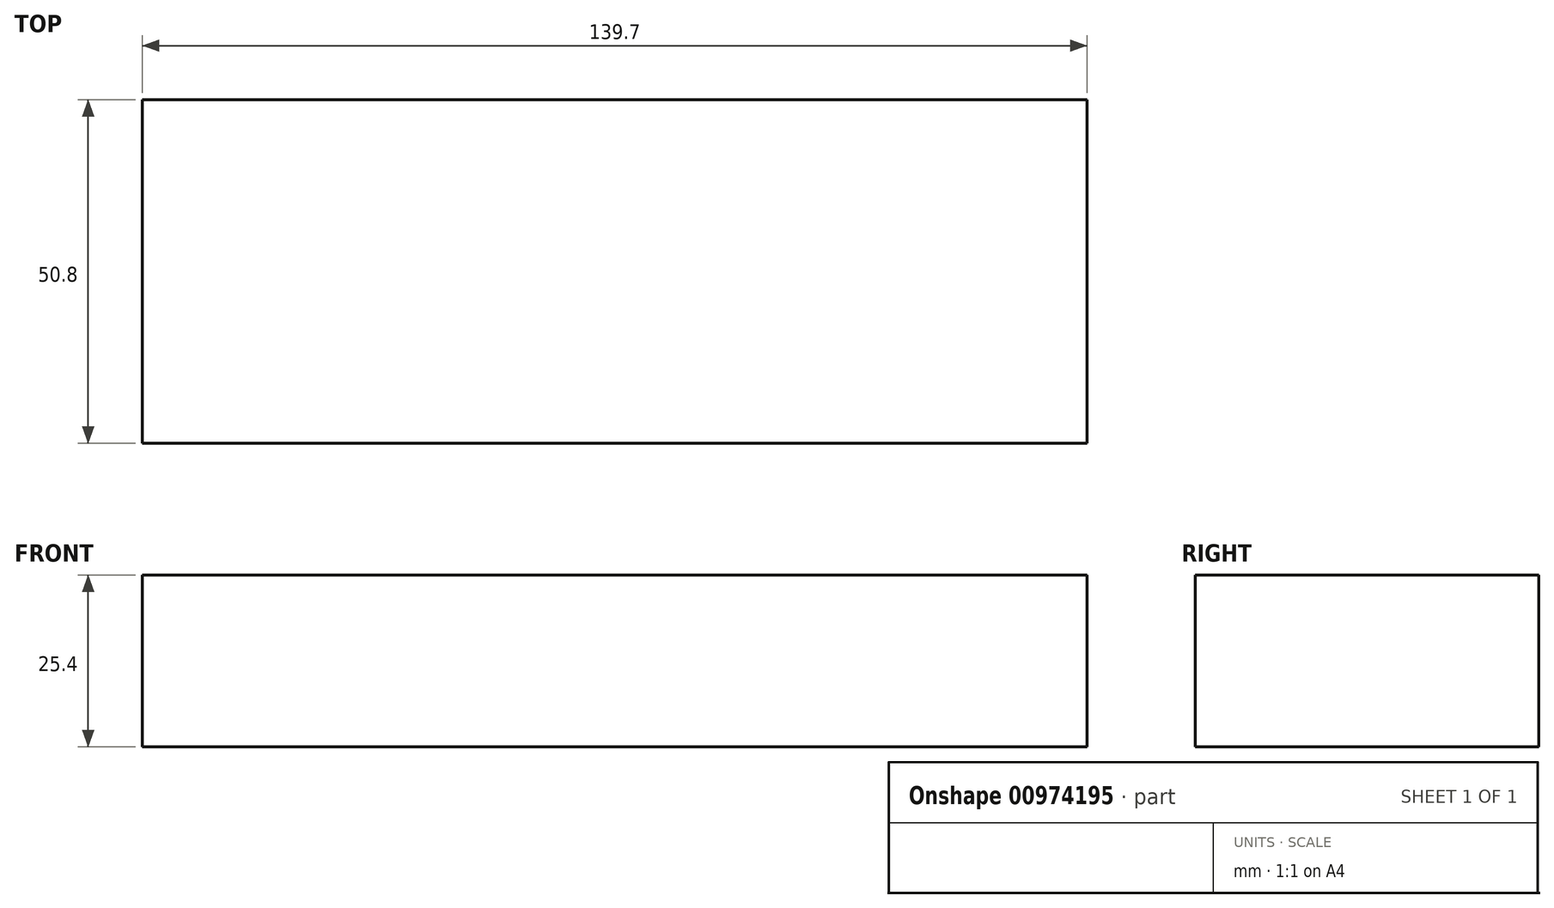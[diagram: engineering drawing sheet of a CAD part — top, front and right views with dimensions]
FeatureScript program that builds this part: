
annotation { "Feature Type Name" : "Feature", "Feature Type Description" : "" }
export const myFeature = defineFeature(function(context is Context, id is Id, definition is map)
    precondition{}
    {
        {
            var Q0;
            Q0=qCreatedBy(makeId("Right.planeOp"),FACE);
            var sketch = newSketch(context, id + "F0", { "sketchPlane" : qUnion([Q0])});
            skLineSegment(sketch, "E0.bottom", {"start": v(25.4, -12.7) * mm, "end": v(-25.4, -12.7) * mm});
            skLineSegment(sketch, "E0.top", {"start": v(25.4, 12.7) * mm, "end": v(-25.4, 12.7) * mm});
            skLineSegment(sketch, "E0.left", {"start": v(25.4, -12.7) * mm, "end": v(25.4, 12.7) * mm});
            skLineSegment(sketch, "E0.right", {"start": v(-25.4, -12.7) * mm, "end": v(-25.4, 12.7) * mm});
            skPoint(sketch, "E0.middle", {"position": v(0, 0) * mm});
            skSolve(sketch);
        }
        {
            var Q0;
            Q0=makeQuery(id+"F0.imprint","IMPRINT",FACE,{"disambiguationData":[TD([[makeQuery(id+"F0.imprint","IMPRINT",EDGE,{"derivedFrom":sQuery(id+"F0.wireOp",EDGE,"E0.bottom")}),-1.0]])]});
            extrude(context, id + "F1", {"entities" : qUnion([Q0]), "depth" : 139.7 * mm, "offsetDistance" : 25.4 * mm});
        }
    });
